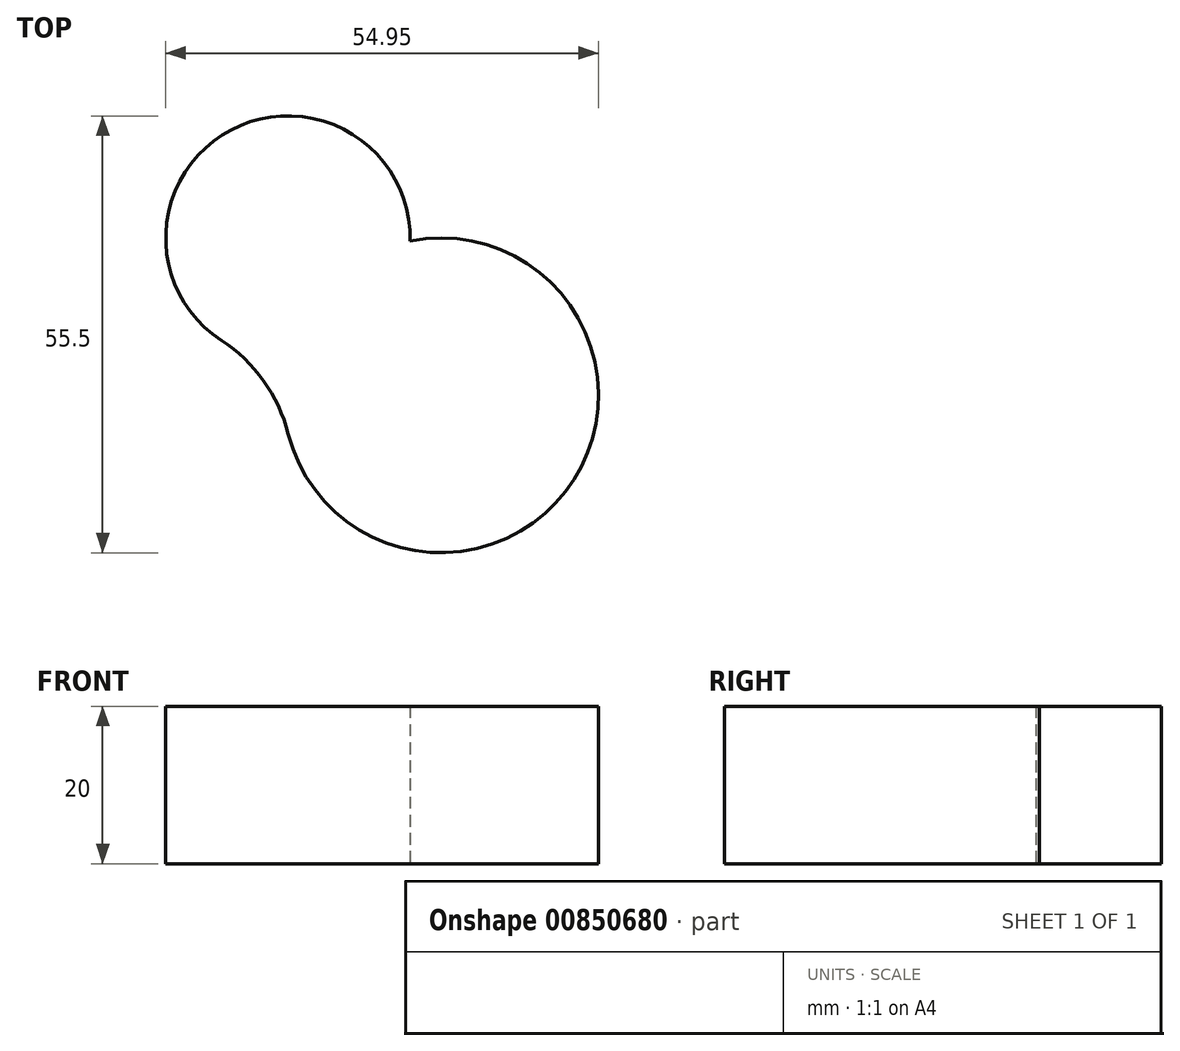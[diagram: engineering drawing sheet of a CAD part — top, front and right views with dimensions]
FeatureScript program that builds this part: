
annotation { "Feature Type Name" : "Feature", "Feature Type Description" : "" }
export const myFeature = defineFeature(function(context is Context, id is Id, definition is map)
    precondition{}
    {
        {
            var Q0;
            Q0=qCreatedBy(makeId("Top.planeOp"),FACE);
            var sketch = newSketch(context, id + "F0", { "sketchPlane" : qUnion([Q0])});
            skArc(sketch, "E0", {"start": v(-19.5, 4.47) * mm, "mid": v(13.94, -14.34) * mm, "end": v(-3.92, 19.61) * mm});
            skArc(sketch, "E1", {"start": v(-3.92, 19.61) * mm, "mid": v(-30.24, 31.1) * mm, "end": v(-19.5, 4.47) * mm});
            skSolve(sketch);
        }
        {
            var Q0;
            Q0=makeQuery(id+"F0.imprint","IMPRINT",FACE,{"disambiguationData":[TD([[makeQuery(id+"F0.imprint","IMPRINT",EDGE,{"derivedFrom":sQuery(id+"F0.wireOp",EDGE,"E0")}),1.0]])]});
            extrude(context, id + "F1", {"entities" : qUnion([Q0]), "depth" : 20 * mm, "offsetDistance" : 25 * mm});
        }
        {
            var Q0;
            {var subQ0=sQuery(id+"F0.wireOp",EDGE,"E1");var subQ1=sQuery(id+"F0.wireOp",EDGE,"E0");Q0=makeQuery(id+"F1.opExtrude","SWEPT_EDGE",EDGE,{"disambiguationData":[OSD([subQ1,subQ0]),TDD([makeQuery(id+"F0.imprint","INTERSECT",VERTEX,{"disambiguationData":[OD(0.0)],"derivedFrom":[subQ1,subQ0]})])]});}
            fillet(context, id + "F2", {"entities" : qUnion([Q0]), "radius" : 20 * mm, "tangentPropagation" : true, "allowEdgeOverflow" : false});
        }
        {
            var Q0;
            Q0=makeQuery(id+"F1.opExtrude","CAP_FACE",FACE,{"disambiguationData":[OSD([sQuery(id+"F0.wireOp",EDGE,"E0"),sQuery(id+"F0.wireOp",EDGE,"E1")])],"isStart":false});
            var sketch = newSketch(context, id + "F3", { "sketchPlane" : qUnion([Q0])});
            skCircle(sketch, "E2", {"center": v(-13.22, 10.73) * mm, "radius": 4 * mm});
            skLineSegment(sketch, "E3", {"start": v(-3.92, 19.61) * mm, "end": v(-22.52, 1.84) * mm, "construction": true});
            skSolve(sketch);
        }
        {
            var Q0;
            Q0=sQuery(id+"F3.wireOp",EDGE,"E2");
            extrude(context, id + "F4", {"bodyType" : ToolBodyType.SURFACE, "surfaceEntities" : qUnion([Q0]), "depth" : 25 * mm, "offsetDistance" : 25 * mm});
        }
    });
